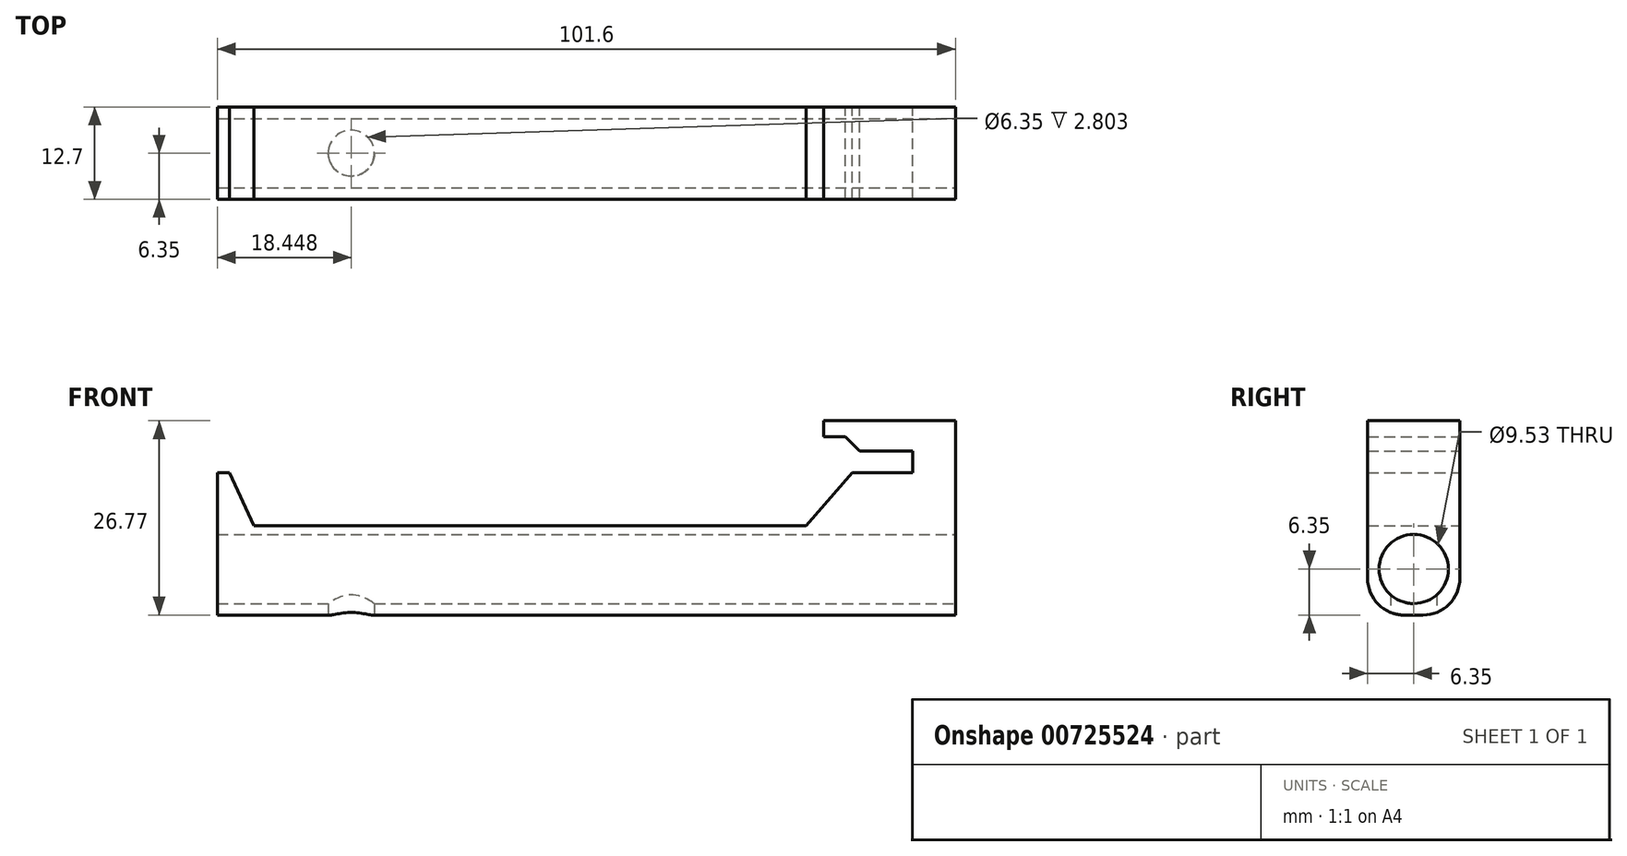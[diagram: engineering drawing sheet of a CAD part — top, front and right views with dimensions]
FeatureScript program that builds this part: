
annotation { "Feature Type Name" : "Feature", "Feature Type Description" : "" }
export const myFeature = defineFeature(function(context is Context, id is Id, definition is map)
    precondition{}
    {
        {
            var Q0;
            Q0=qCreatedBy(makeId("Front.planeOp"),FACE);
            var sketch = newSketch(context, id + "F0", { "sketchPlane" : qUnion([Q0])});
            skLineSegment(sketch, "E0", {"start": v(0, 0) * mm, "end": v(0, 20.42) * mm});
            skLineSegment(sketch, "E1", {"start": v(0, 20.42) * mm, "end": v(-18.14, 20.42) * mm});
            skLineSegment(sketch, "E2", {"start": v(-18.14, 20.42) * mm, "end": v(-18.14, 18.24) * mm});
            skLineSegment(sketch, "E3", {"start": v(-18.14, 18.24) * mm, "end": v(-15.17, 18.24) * mm});
            skLineSegment(sketch, "E4", {"start": v(-15.17, 18.24) * mm, "end": v(-13.19, 16.26) * mm});
            skLineSegment(sketch, "E5", {"start": v(-13.19, 16.26) * mm, "end": v(-5.85, 16.26) * mm});
            skLineSegment(sketch, "E6", {"start": v(-5.85, 16.26) * mm, "end": v(-5.85, 13.29) * mm});
            skLineSegment(sketch, "E7", {"start": v(-5.85, 13.29) * mm, "end": v(-14.18, 13.29) * mm});
            skLineSegment(sketch, "E8", {"start": v(-14.18, 13.29) * mm, "end": v(-20.52, 5.95) * mm});
            skLineSegment(sketch, "E9", {"start": v(-20.52, 5.95) * mm, "end": v(-62.48, 5.95) * mm});
            skLineSegment(sketch, "E10", {"start": v(-99.92, 13.29) * mm, "end": v(-101.6, 13.29) * mm});
            skLineSegment(sketch, "E11", {"start": v(-101.6, 13.29) * mm, "end": v(-101.6, 0) * mm});
            skLineSegment(sketch, "E12", {"start": v(-101.6, 0) * mm, "end": v(0, 0) * mm});
            skLineSegment(sketch, "E13", {"start": v(-62.48, 5.95) * mm, "end": v(-96.54, 5.95) * mm});
            skLineSegment(sketch, "E14", {"start": v(-96.54, 5.95) * mm, "end": v(-99.92, 13.29) * mm});
            skPoint(sketch, "E15.orphan", {"position": v(-67.44, 13.29) * mm});
            skSolve(sketch);
        }
        {
            var Q0;
            Q0=makeQuery(id+"F0.imprint","IMPRINT",FACE,{"disambiguationData":[TD([[makeQuery(id+"F0.imprint","IMPRINT",EDGE,{"derivedFrom":sQuery(id+"F0.wireOp",EDGE,"E0")}),1.0]])]});
            extrude(context, id + "F1", {"entities" : qUnion([Q0]), "depth" : 12.7 * mm, "offsetDistance" : 25.4 * mm});
        }
        {
            var Q0;
            Q0=makeQuery(id+"F1.opExtrude","SWEPT_FACE",FACE,{"disambiguationData":[OSD([sQuery(id+"F0.wireOp",EDGE,"E12")])]});
            var sketch = newSketch(context, id + "F2", { "sketchPlane" : qUnion([Q0])});
            skSolve(sketch);
        }
        {
            var Q0;
            Q0 = qSketchRegion(id + "F2", true);
            var Q1;
            {var subQ0=sQuery(id+"F0.wireOp",EDGE,"E12");Q1=makeQuery(id+"F2.imprint","IMPRINT",FACE,{"disambiguationData":[TD([[makeQuery(id+"F2.imprint","IMPRINT",EDGE,{"derivedFrom":makeQuery(id+"F1.opExtrude","CAP_EDGE",EDGE,{"disambiguationData":[OSD([subQ0])],"isStart":true})}),1.0]])]});}
            extrude(context, id + "F3", {"entities" : qUnion([Q0, Q1]), "operationType" : NewBodyOperationType.ADD, "depth" : 6.35 * mm, "offsetDistance" : 25.4 * mm});
        }
        {
            var Q0;
            {var subQ0=sQuery(id+"F0.wireOp",EDGE,"E12");Q0=makeQuery(id+"F3.opExtrude","CAP_EDGE",EDGE,{"disambiguationData":[OSD([subQ0]),TDD([makeQuery(id+"F2.imprint","IMPRINT",EDGE,{"derivedFrom":makeQuery(id+"F1.opExtrude","CAP_EDGE",EDGE,{"disambiguationData":[OSD([subQ0])],"isStart":false})})])],"isStart":false});}
            var Q1;
            {var subQ0=sQuery(id+"F0.wireOp",EDGE,"E12");Q1=makeQuery(id+"F3.opExtrude","CAP_EDGE",EDGE,{"disambiguationData":[OSD([subQ0]),TDD([makeQuery(id+"F2.imprint","IMPRINT",EDGE,{"derivedFrom":makeQuery(id+"F1.opExtrude","CAP_EDGE",EDGE,{"disambiguationData":[OSD([subQ0])],"isStart":true})})])],"isStart":false});}
            fillet(context, id + "F4", {"entities" : qUnion([Q0, Q1]), "radius" : 5.08 * mm, "tangentPropagation" : true, "allowEdgeOverflow" : false});
        }
        {
            var Q0;
            {var subQ0=sQuery(id+"F0.wireOp",EDGE,"E0");Q0=makeQuery(id+"F3.boolean.opBoolean","MERGE",FACE,{"derivedFrom":[makeQuery(id+"F1.opExtrude","SWEPT_FACE",FACE,{"disambiguationData":[OSD([subQ0])]}),makeQuery(id+"F3.opExtrude","SWEPT_FACE",FACE,{"disambiguationData":[OSD([subQ0,sQuery(id+"F0.wireOp",EDGE,"E12")])]})]});}
            var sketch = newSketch(context, id + "F5", { "sketchPlane" : qUnion([Q0])});
            skPoint(sketch, "E16", {"position": v(-6.35, 0) * mm});
            skPoint(sketch, "E16.positionSnap0", {"position": v(-6.35, -6.35) * mm});
            skSolve(sketch);
        }
        {
            var Q0;
            Q0=sQuery(id+"F5.wireOp",VERTEX,"E16");
            var Q1;
            Q1=makeQuery(id+"F1.opExtrude","SWEPT_BODY",BODY,{"disambiguationData":[OSD([sQuery(id+"F0.wireOp",EDGE,"E0"),sQuery(id+"F0.wireOp",EDGE,"E1"),sQuery(id+"F0.wireOp",EDGE,"E2"),sQuery(id+"F0.wireOp",EDGE,"E3"),sQuery(id+"F0.wireOp",EDGE,"E4"),sQuery(id+"F0.wireOp",EDGE,"E5"),sQuery(id+"F0.wireOp",EDGE,"E6"),sQuery(id+"F0.wireOp",EDGE,"E7"),sQuery(id+"F0.wireOp",EDGE,"E8"),sQuery(id+"F0.wireOp",EDGE,"E9"),sQuery(id+"F0.wireOp",EDGE,"E11"),sQuery(id+"F0.wireOp",EDGE,"E12"),sQuery(id+"F0.wireOp",EDGE,"E13"),sQuery(id+"F0.wireOp",EDGE,"E14"),sQuery(id+"F0.wireOp",EDGE,"E10")])]});
            hole(context, id + "F6", {"style" : HoleStyle.SIMPLE, "endStyle" : HoleEndStyle.THROUGH, "holeDiameter" : 9.52 * mm, "majorDiameter" : 6.35 * mm, "isTappedThrough" : true, "tappedDepth" : 12.7 * mm, "tapClearance" : 3, "locations" : qUnion([Q0]), "scope" : qUnion([Q1])});
        }
        {
            var Q0;
            Q0=makeQuery(id+"F3.opExtrude","CAP_FACE",FACE,{"disambiguationData":[OSD([sQuery(id+"F0.wireOp",EDGE,"E0"),sQuery(id+"F0.wireOp",EDGE,"E11"),sQuery(id+"F0.wireOp",EDGE,"E12")])],"isStart":false});
            var sketch = newSketch(context, id + "F7", { "sketchPlane" : qUnion([Q0])});
            skPoint(sketch, "E17", {"position": v(-83.15, 6.35) * mm});
            skPoint(sketch, "E17.positionSnap0", {"position": v(-101.6, 6.35) * mm});
            skSolve(sketch);
        }
        {
            var Q0;
            Q0=sQuery(id+"F7.wireOp",VERTEX,"E17");
            var Q1;
            Q1=makeQuery(id+"F1.opExtrude","SWEPT_BODY",BODY,{"disambiguationData":[OSD([sQuery(id+"F0.wireOp",EDGE,"E0"),sQuery(id+"F0.wireOp",EDGE,"E1"),sQuery(id+"F0.wireOp",EDGE,"E2"),sQuery(id+"F0.wireOp",EDGE,"E3"),sQuery(id+"F0.wireOp",EDGE,"E4"),sQuery(id+"F0.wireOp",EDGE,"E5"),sQuery(id+"F0.wireOp",EDGE,"E6"),sQuery(id+"F0.wireOp",EDGE,"E7"),sQuery(id+"F0.wireOp",EDGE,"E8"),sQuery(id+"F0.wireOp",EDGE,"E9"),sQuery(id+"F0.wireOp",EDGE,"E11"),sQuery(id+"F0.wireOp",EDGE,"E12"),sQuery(id+"F0.wireOp",EDGE,"E13"),sQuery(id+"F0.wireOp",EDGE,"E14"),sQuery(id+"F0.wireOp",EDGE,"E10")])]});
            hole(context, id + "F8", {"style" : HoleStyle.SIMPLE, "endStyle" : HoleEndStyle.BLIND, "holeDiameter" : 6.35 * mm, "majorDiameter" : 6.35 * mm, "holeDepth" : 5.08 * mm, "isTappedThrough" : true, "tappedDepth" : 12.7 * mm, "tapClearance" : 3, "locations" : qUnion([Q0]), "scope" : qUnion([Q1])});
        }
    });
